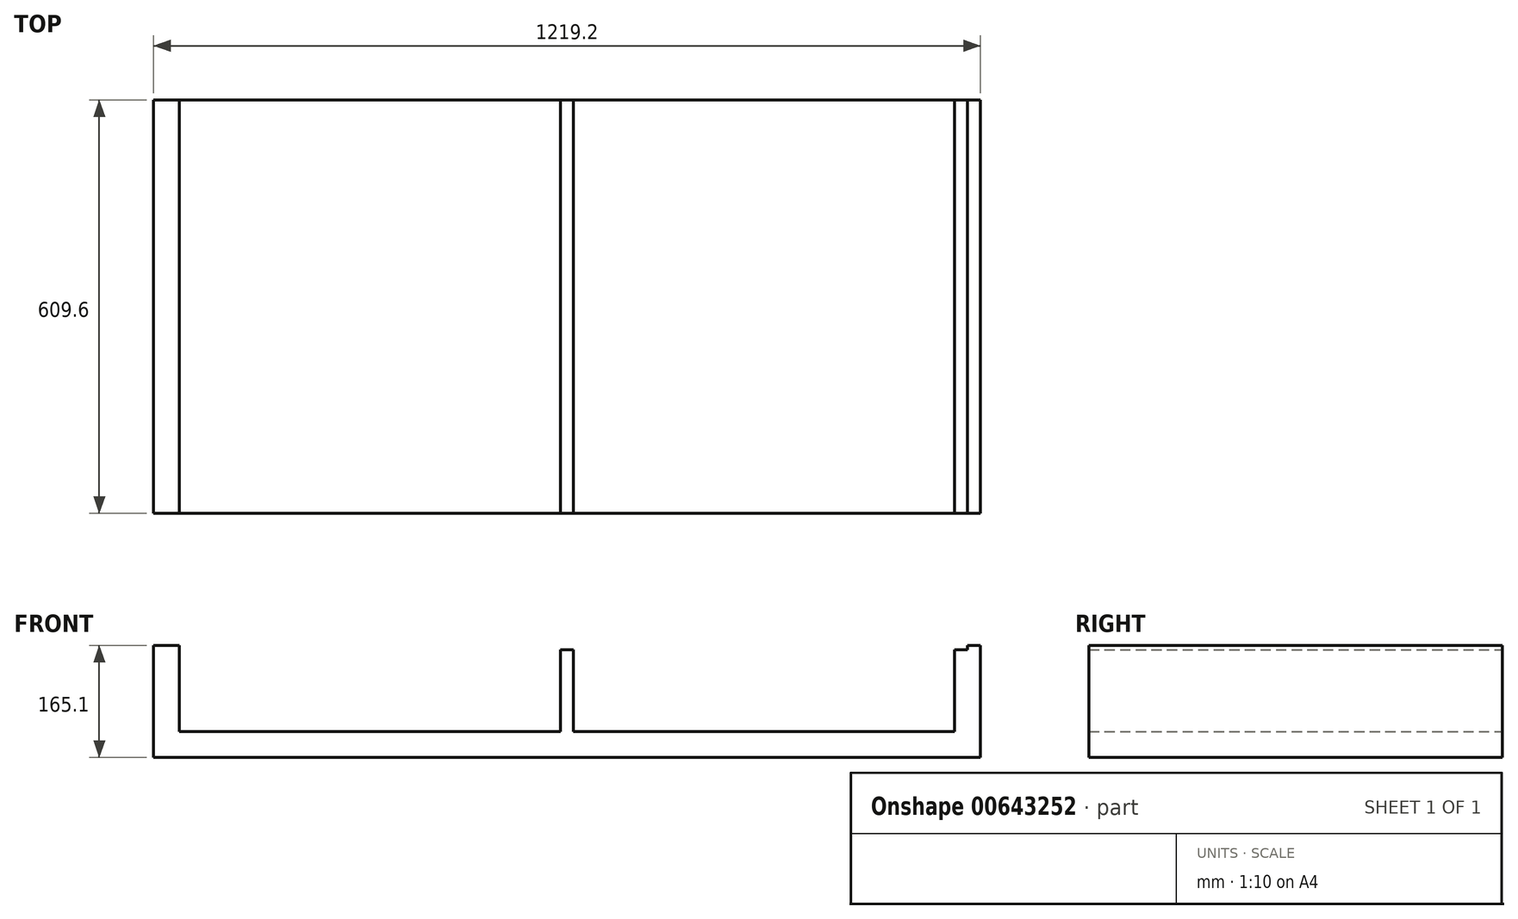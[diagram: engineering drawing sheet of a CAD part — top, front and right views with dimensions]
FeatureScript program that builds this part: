
annotation { "Feature Type Name" : "Feature", "Feature Type Description" : "" }
export const myFeature = defineFeature(function(context is Context, id is Id, definition is map)
    precondition{}
    {
        {
            var Q0;
            Q0=qCreatedBy(makeId("Front.planeOp"),FACE);
            var sketch = newSketch(context, id + "F0", { "sketchPlane" : qUnion([Q0])});
            skLineSegment(sketch, "E0", {"start": v(-609.6, 0) * mm, "end": v(609.6, 0) * mm});
            skLineSegment(sketch, "E1", {"start": v(-609.6, 0) * mm, "end": v(-609.6, 165.1) * mm});
            skLineSegment(sketch, "E2", {"start": v(-609.6, 165.1) * mm, "end": v(-571.5, 165.1) * mm});
            skLineSegment(sketch, "E3", {"start": v(-571.5, 165.1) * mm, "end": v(-571.5, 38.1) * mm});
            skLineSegment(sketch, "E4", {"start": v(-571.5, 38.1) * mm, "end": v(571.5, 38.1) * mm});
            skLineSegment(sketch, "E5", {"start": v(571.5, 38.1) * mm, "end": v(571.5, 158.75) * mm});
            skLineSegment(sketch, "E6", {"start": v(590.55, 165.1) * mm, "end": v(609.6, 165.1) * mm});
            skLineSegment(sketch, "E7", {"start": v(609.6, 165.1) * mm, "end": v(609.6, 0) * mm});
            skLineSegment(sketch, "E8.bottom", {"start": v(-9.52, 38.1) * mm, "end": v(9.52, 38.1) * mm});
            skLineSegment(sketch, "E8.top", {"start": v(-9.53, 158.75) * mm, "end": v(9.52, 158.75) * mm});
            skLineSegment(sketch, "E8.left", {"start": v(-9.52, 38.1) * mm, "end": v(-9.53, 158.75) * mm});
            skLineSegment(sketch, "E8.right", {"start": v(9.52, 38.1) * mm, "end": v(9.52, 158.75) * mm});
            skLineSegment(sketch, "E9", {"start": v(571.5, 158.75) * mm, "end": v(590.55, 158.75) * mm});
            skLineSegment(sketch, "E10", {"start": v(590.55, 158.75) * mm, "end": v(590.55, 165.1) * mm});
            skPoint(sketch, "E11.orphan", {"position": v(571.5, 165.1) * mm});
            skSolve(sketch);
        }
        {
            var Q0;
            Q0 = qSketchRegion(id + "F0", true);
            extrude(context, id + "F1", {"entities" : qUnion([Q0]), "depth" : 609.6 * mm, "offsetDistance" : 25.4 * mm});
        }
    });
